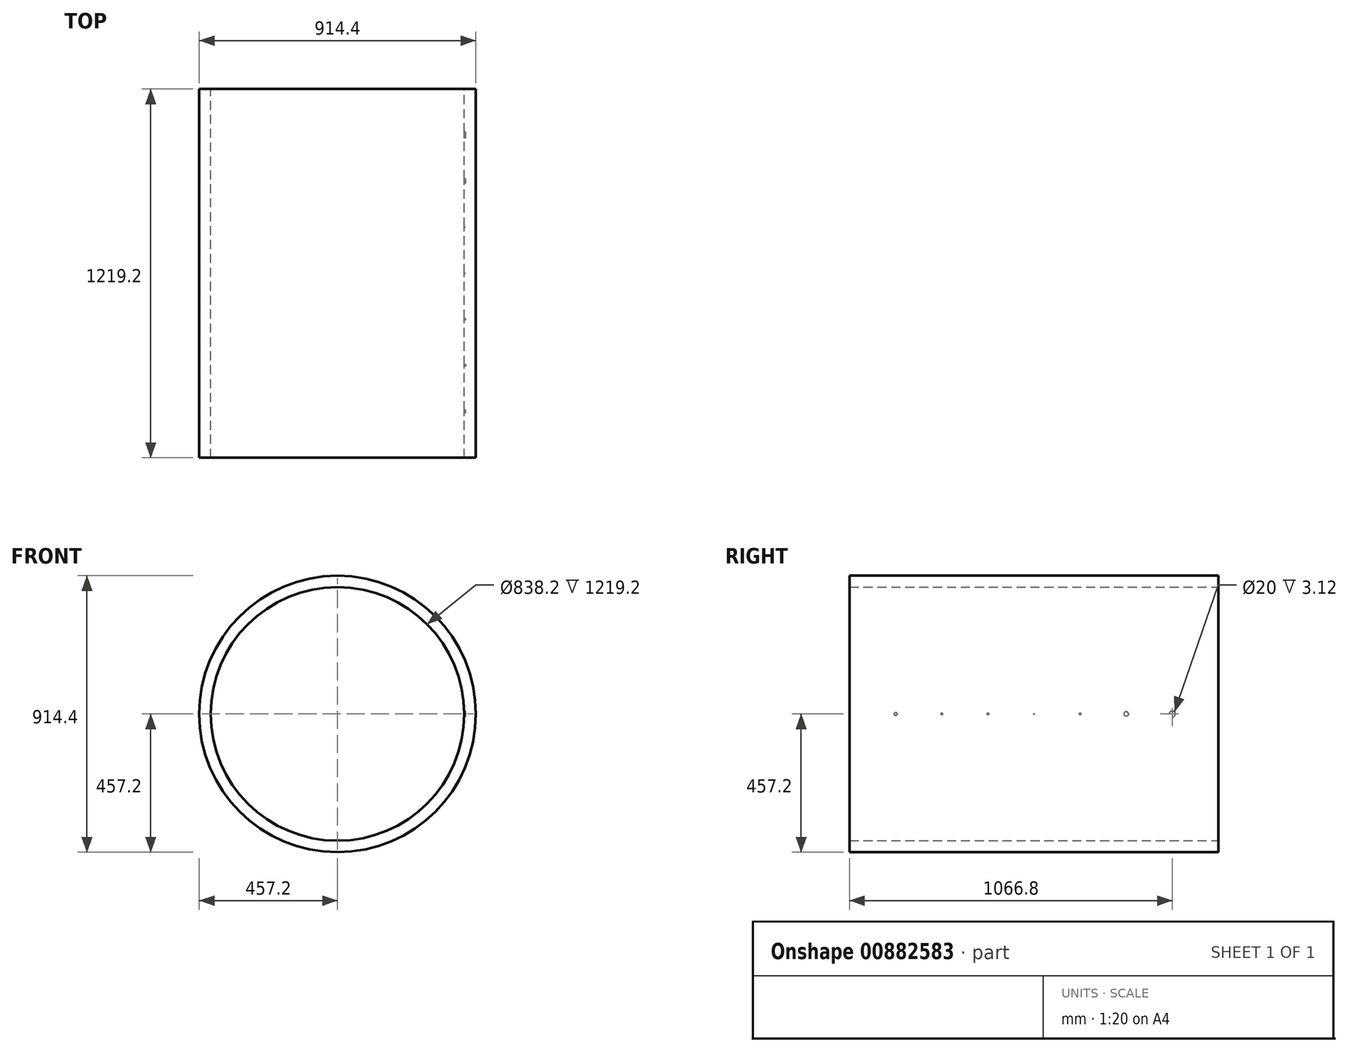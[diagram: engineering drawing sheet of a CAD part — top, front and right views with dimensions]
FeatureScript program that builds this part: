
annotation { "Feature Type Name" : "Feature", "Feature Type Description" : "" }
export const myFeature = defineFeature(function(context is Context, id is Id, definition is map)
    precondition{}
    {
        {
            var Q0;
            Q0=qCreatedBy(makeId("Front.planeOp"),FACE);
            var sketch = newSketch(context, id + "F0", { "sketchPlane" : qUnion([Q0])});
            skCircle(sketch, "E0", {"center": v(0, 0) * mm, "radius": 457.2 * mm});
            skCircle(sketch, "E1", {"center": v(0, 0) * mm, "radius": 419.1 * mm});
            skSolve(sketch);
        }
        {
            var Q0;
            Q0 = qSketchRegion(id + "F0", true);
            extrude(context, id + "F1", {"entities" : qUnion([Q0]), "depth" : 1219.2 * mm, "offsetDistance" : 25.4 * mm});
        }
        {
            var Q0;
            Q0=qCreatedBy(makeId("Top.planeOp"),FACE);
            var sketch = newSketch(context, id + "F2", { "sketchPlane" : qUnion([Q0])});
            skLineSegment(sketch, "E2", {"start": v(419.1, 0) * mm, "end": v(419.1, -1500) * mm, "construction": true});
            skSolve(sketch);
        }
        {
            var Q0;
            Q0=qCreatedBy(makeId("Right.planeOp"),FACE);
            var Q1;
            Q1=sQuery(id+"F2.wireOp",EDGE,"E2");
            cPlane(context, id + "F3", {"entities" : qUnion([Q0, Q1]), "cplaneType" : CPlaneType.LINE_ANGLE, "offset" : 25.4 * mm, "angle" : 0 * degree, "width" : 152.4 * mm, "height" : 152.4 * mm});
        }
        {
            var Q0;
            Q0=qCreatedBy(id+"F3.planeOp",FACE);
            cPlane(context, id + "F4", {"entities" : qUnion([Q0]), "cplaneType" : CPlaneType.OFFSET, "offset" : 100 * mm, "width" : 152.4 * mm, "height" : 152.4 * mm});
        }
        {
            var Q0;
            Q0=qCreatedBy(id+"F4.planeOp",FACE);
            var sketch = newSketch(context, id + "F5", { "sketchPlane" : qUnion([Q0])});
            skCircle(sketch, "E3", {"center": v(152.4, 0) * mm, "radius": 10 * mm});
            skSolve(sketch);
        }
        {
            var Q0;
            Q0 = qSketchRegion(id + "F5", true);
            extrude(context, id + "F6", {"entities" : qUnion([Q0]), "operationType" : NewBodyOperationType.REMOVE, "oppositeDirection" : true, "depth" : 103 * mm, "offsetDistance" : 25.4 * mm});
        }
        {
            var Q0;
            Q0=qCreatedBy(id+"F4.planeOp",FACE);
            var sketch = newSketch(context, id + "F7", { "sketchPlane" : qUnion([Q0])});
            skCircle(sketch, "E4", {"center": v(304.8, 0) * mm, "radius": 7.5 * mm});
            skSolve(sketch);
        }
        {
            var Q0;
            Q0=makeQuery(id+"F7.imprint","IMPRINT",FACE,{"disambiguationData":[TD([[makeQuery(id+"F7.imprint","IMPRINT",EDGE,{"derivedFrom":sQuery(id+"F7.wireOp",EDGE,"E4")}),1.0]])]});
            extrude(context, id + "F8", {"entities" : qUnion([Q0]), "operationType" : NewBodyOperationType.REMOVE, "oppositeDirection" : true, "depth" : 103 * mm, "offsetDistance" : 25.4 * mm});
        }
        {
            var Q0;
            Q0=qCreatedBy(id+"F4.planeOp",FACE);
            var sketch = newSketch(context, id + "F9", { "sketchPlane" : qUnion([Q0])});
            skCircle(sketch, "E5", {"center": v(457.2, 0) * mm, "radius": 2.5 * mm});
            skSolve(sketch);
        }
        {
            var Q0;
            Q0 = qSketchRegion(id + "F9", true);
            extrude(context, id + "F10", {"entities" : qUnion([Q0]), "operationType" : NewBodyOperationType.REMOVE, "oppositeDirection" : true, "depth" : 101 * mm, "offsetDistance" : 25.4 * mm});
        }
        {
            var Q0;
            Q0=qCreatedBy(id+"F4.planeOp",FACE);
            var sketch = newSketch(context, id + "F11", { "sketchPlane" : qUnion([Q0])});
            skCircle(sketch, "E6", {"center": v(609.6, 0) * mm, "radius": 1 * mm});
            skSolve(sketch);
        }
        {
            var Q0;
            Q0 = qSketchRegion(id + "F11", true);
            extrude(context, id + "F12", {"entities" : qUnion([Q0]), "operationType" : NewBodyOperationType.REMOVE, "oppositeDirection" : true, "depth" : 102 * mm, "offsetDistance" : 25.4 * mm});
        }
        {
            var Q0;
            Q0=qCreatedBy(id+"F4.planeOp",FACE);
            var sketch = newSketch(context, id + "F13", { "sketchPlane" : qUnion([Q0])});
            skCircle(sketch, "E7", {"center": v(762, 0) * mm, "radius": 2.5 * mm});
            skSolve(sketch);
        }
        {
            var Q0;
            Q0 = qSketchRegion(id + "F13", true);
            extrude(context, id + "F14", {"entities" : qUnion([Q0]), "operationType" : NewBodyOperationType.REMOVE, "oppositeDirection" : true, "depth" : 103 * mm, "offsetDistance" : 25.4 * mm});
        }
        {
            var Q0;
            Q0=qCreatedBy(id+"F4.planeOp",FACE);
            var sketch = newSketch(context, id + "F15", { "sketchPlane" : qUnion([Q0])});
            skCircle(sketch, "E8", {"center": v(914.4, 0) * mm, "radius": 2.5 * mm});
            skSolve(sketch);
        }
        {
            var Q0;
            Q0 = qSketchRegion(id + "F15", true);
            extrude(context, id + "F16", {"entities" : qUnion([Q0]), "operationType" : NewBodyOperationType.REMOVE, "oppositeDirection" : true, "depth" : 105 * mm, "offsetDistance" : 25.4 * mm});
        }
        {
            var Q0;
            Q0=qCreatedBy(id+"F4.planeOp",FACE);
            var sketch = newSketch(context, id + "F17", { "sketchPlane" : qUnion([Q0])});
            skCircle(sketch, "E9", {"center": v(1066.8, 0) * mm, "radius": 5 * mm});
            skSolve(sketch);
        }
        {
            var Q0;
            Q0 = qSketchRegion(id + "F17", true);
            extrude(context, id + "F18", {"entities" : qUnion([Q0]), "operationType" : NewBodyOperationType.REMOVE, "oppositeDirection" : true, "depth" : 103 * mm, "offsetDistance" : 25.4 * mm});
        }
    });
